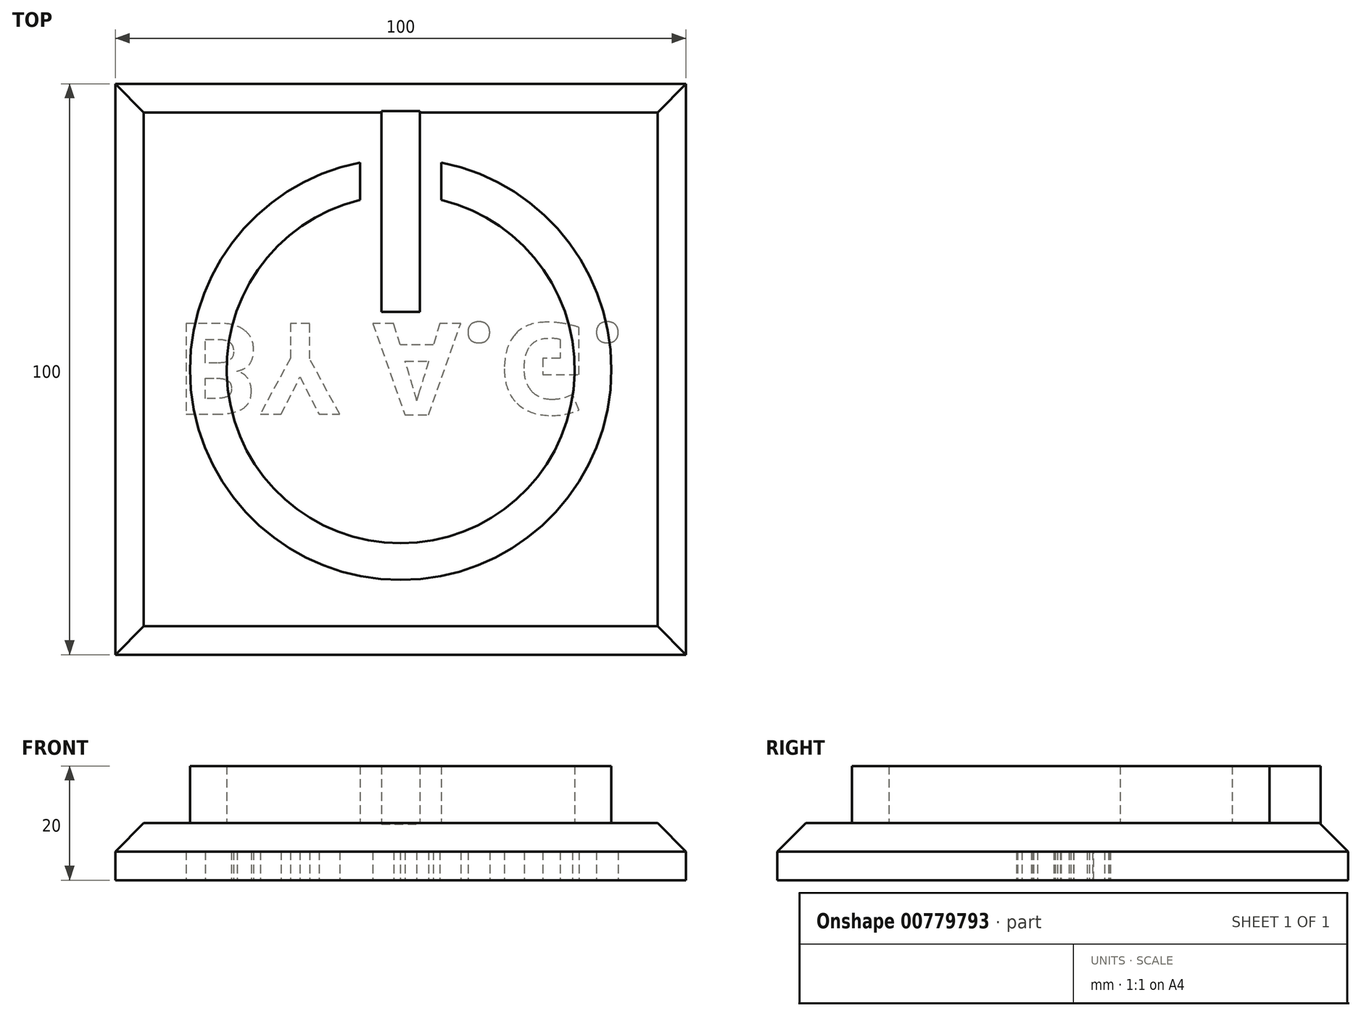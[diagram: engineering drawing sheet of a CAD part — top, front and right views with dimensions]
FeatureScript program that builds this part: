
annotation { "Feature Type Name" : "Feature", "Feature Type Description" : "" }
export const myFeature = defineFeature(function(context is Context, id is Id, definition is map)
    precondition{}
    {
        {
            var Q0;
            Q0=qCreatedBy(makeId("Top.planeOp"),FACE);
            var sketch = newSketch(context, id + "F0", { "sketchPlane" : qUnion([Q0])});
            skLineSegment(sketch, "E0.bottom", {"start": v(-50, 50) * mm, "end": v(50, 50) * mm});
            skLineSegment(sketch, "E0.top", {"start": v(-50, -50) * mm, "end": v(50, -50) * mm});
            skLineSegment(sketch, "E0.left", {"start": v(-50, 50) * mm, "end": v(-50, -50) * mm});
            skLineSegment(sketch, "E0.right", {"start": v(50, 50) * mm, "end": v(50, -50) * mm});
            skPoint(sketch, "E0.middle", {"position": v(0, 0) * mm});
            skSolve(sketch);
        }
        {
            var Q0;
            Q0 = qSketchRegion(id + "F0", true);
            extrude(context, id + "F1", {"entities" : qUnion([Q0]), "depth" : 10 * mm, "offsetDistance" : 25 * mm});
        }
        {
            var Q0;
            Q0=makeQuery(id+"F1.opExtrude","CAP_FACE",FACE,{"disambiguationData":[OSD([sQuery(id+"F0.wireOp",EDGE,"E0.bottom"),sQuery(id+"F0.wireOp",EDGE,"E0.top"),sQuery(id+"F0.wireOp",EDGE,"E0.left"),sQuery(id+"F0.wireOp",EDGE,"E0.right")])],"isStart":false});
            var sketch = newSketch(context, id + "F2", { "sketchPlane" : qUnion([Q0])});
            skArc(sketch, "E1", {"start": v(-7.12, 36.22) * mm, "mid": v(0, -36.91) * mm, "end": v(7.12, 36.22) * mm});
            skArc(sketch, "E2", {"start": v(-7.12, 29.65) * mm, "mid": v(0, -30.5) * mm, "end": v(7.12, 29.65) * mm});
            skLineSegment(sketch, "E3", {"start": v(-7.12, 36.22) * mm, "end": v(-7.12, 29.65) * mm});
            skLineSegment(sketch, "E4.MirrorCS", {"start": v(7.12, 36.22) * mm, "end": v(7.12, 29.65) * mm});
            skLineSegment(sketch, "E5.bottom", {"start": v(-3.36, 10.07) * mm, "end": v(3.36, 10.07) * mm});
            skLineSegment(sketch, "E5.left", {"start": v(-3.36, 10.07) * mm, "end": v(-3.36, 45.2) * mm});
            skLineSegment(sketch, "E5.right", {"start": v(3.36, 10.07) * mm, "end": v(3.36, 45.2) * mm});
            skPoint(sketch, "E5.middle", {"position": v(0, 33.63) * mm});
            skLineSegment(sketch, "E6", {"start": v(-3.36, 45.2) * mm, "end": v(3.36, 45.2) * mm});
            skPoint(sketch, "E5.top.start.orphan", {"position": v(-3.36, 57.2) * mm});
            skPoint(sketch, "E7.orphan", {"position": v(3.36, 57.2) * mm});
            skSolve(sketch);
        }
        {
            var Q0;
            Q0 = qSketchRegion(id + "F2", true);
            extrude(context, id + "F3", {"entities" : qUnion([Q0]), "operationType" : NewBodyOperationType.ADD, "depth" : 10 * mm, "offsetDistance" : 25 * mm});
        }
        {
            var Q0;
            Q0=makeQuery(id+"F1.opExtrude","CAP_EDGE",EDGE,{"disambiguationData":[OSD([sQuery(id+"F0.wireOp",EDGE,"E0.left")])],"isStart":false});
            var Q1;
            Q1=makeQuery(id+"F1.opExtrude","CAP_EDGE",EDGE,{"disambiguationData":[OSD([sQuery(id+"F0.wireOp",EDGE,"E0.bottom")])],"isStart":false});
            var Q2;
            Q2=makeQuery(id+"F1.opExtrude","CAP_EDGE",EDGE,{"disambiguationData":[OSD([sQuery(id+"F0.wireOp",EDGE,"E0.top")])],"isStart":false});
            var Q3;
            Q3=makeQuery(id+"F1.opExtrude","CAP_EDGE",EDGE,{"disambiguationData":[OSD([sQuery(id+"F0.wireOp",EDGE,"E0.right")])],"isStart":false});
            chamfer(context, id + "F4", {"entities" : qUnion([Q0, Q1, Q2, Q3]), "width" : 5 * mm, "tangentPropagation" : true});
        }
        {
            var Q0;
            Q0=makeQuery(id+"F1.opExtrude","CAP_FACE",FACE,{"disambiguationData":[OSD([sQuery(id+"F0.wireOp",EDGE,"E0.bottom"),sQuery(id+"F0.wireOp",EDGE,"E0.top"),sQuery(id+"F0.wireOp",EDGE,"E0.left"),sQuery(id+"F0.wireOp",EDGE,"E0.right")])],"isStart":true});
            var sketch = newSketch(context, id + "F5", { "sketchPlane" : qUnion([Q0])});
            skLineSegment(sketch, "E8.bottom", {"start": v(-39.58, 8.03) * mm, "end": v(39.58, 8.03) * mm, "construction": true});
            skLineSegment(sketch, "E8.top", {"start": v(-39.58, -8.03) * mm, "end": v(39.58, -8.03) * mm, "construction": true});
            skLineSegment(sketch, "E8.left", {"start": v(-39.58, 8.03) * mm, "end": v(-39.58, -8.03) * mm, "construction": true});
            skLineSegment(sketch, "E8.right", {"start": v(39.58, 8.03) * mm, "end": v(39.58, -8.03) * mm, "construction": true});
            skPoint(sketch, "E8.middle", {"position": v(0, 0) * mm});
            skText(sketch, "E9", { "text": "BY A.G.", "fontName": "OpenSans-Bold.ttf"});
            const initialGuessF5  = {"E9": [-0.03958, -0.00803, 1, 0, 0.01606]};
            skSetInitialGuess(sketch, initialGuessF5);
            skSolve(sketch);
        }
        {
            var Q0;
            Q0 = qSketchRegion(id + "F5", true);
            extrude(context, id + "F6", {"entities" : qUnion([Q0]), "operationType" : NewBodyOperationType.REMOVE, "oppositeDirection" : true, "depth" : 5 * mm, "offsetDistance" : 25 * mm});
        }
    });
